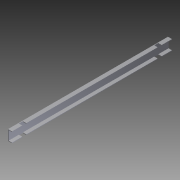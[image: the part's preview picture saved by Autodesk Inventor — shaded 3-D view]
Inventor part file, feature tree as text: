
AUTODESK INVENTOR PART (.ipt)
format: ipt  version: 2012 (Build 160160000, 160)  size: 104,960 bytes
history: native  units: in
note: dims shown in document units (in); Inventor stores cm internally (conversion verified against a paired STEP export)
features: extrude x2, sketch x2
ambient origin geometry x8: Origin, YZ Plane, XZ Plane, XY Plane, X Axis, Y Axis, Z Axis, Center Point
bodies: Solid1 (feature_tree)
feature tree (4):
  extrude  "Extrusion1"  Depth=35.0in TaperAngle=0.0deg
  extrude  "Extrusion4"  Depth=0.875in
  sketch  "Sketch1"  dims[d0=0.125in d1=0.125in d2=0.125in d3=2.25in d4=0.875in d5=35.0in d6=0.0in]
  sketch  "Sketch4"  dims[d33=0.75in d34=0.875in d35=3.125in d36=35.0in d37=17.5in d38=1.0in d39=0.0in]
